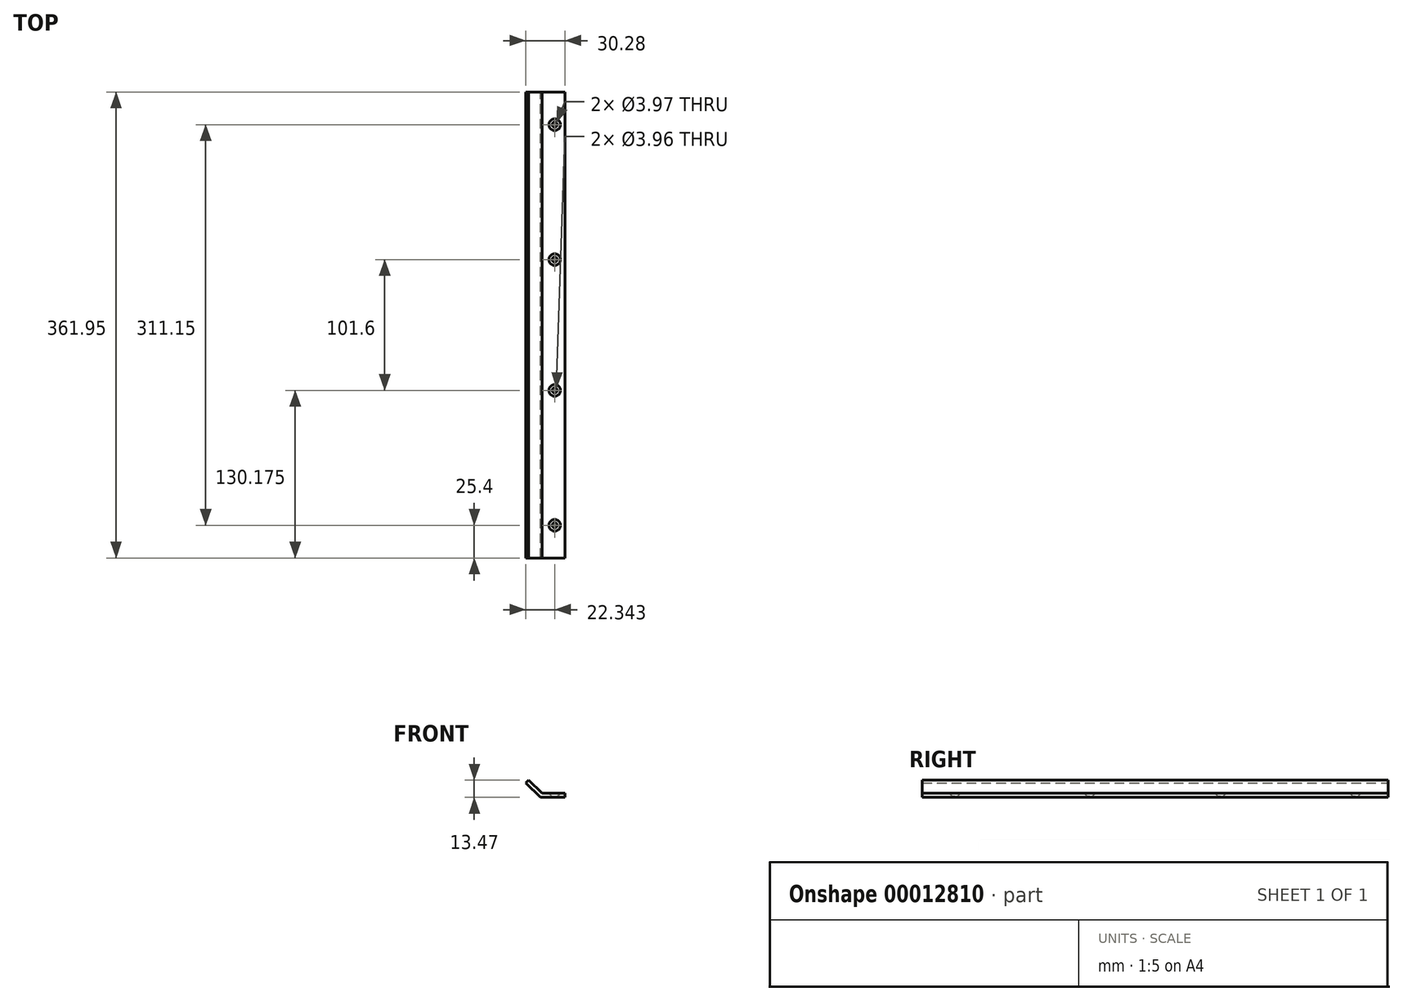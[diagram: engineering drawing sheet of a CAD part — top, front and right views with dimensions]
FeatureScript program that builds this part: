
annotation { "Feature Type Name" : "Feature", "Feature Type Description" : "" }
export const myFeature = defineFeature(function(context is Context, id is Id, definition is map)
    precondition{}
    {
        {
            var Q0;
            Q0=qCreatedBy(makeId("Front.planeOp"),FACE);
            var sketch = newSketch(context, id + "F0", { "sketchPlane" : qUnion([Q0])});
            skLineSegment(sketch, "E0", {"start": v(0, 0) * mm, "end": v(-19.05, 0) * mm});
            skLineSegment(sketch, "E1", {"start": v(-19.05, 0) * mm, "end": v(-30.28, 11.23) * mm});
            skLineSegment(sketch, "E2", {"start": v(-30.28, 11.23) * mm, "end": v(-28.03, 13.47) * mm});
            skLineSegment(sketch, "E3", {"start": v(-28.03, 13.47) * mm, "end": v(-17.73, 3.17) * mm});
            skLineSegment(sketch, "E4", {"start": v(-17.73, 3.17) * mm, "end": v(0, 3.17) * mm});
            skLineSegment(sketch, "E5", {"start": v(0, 3.17) * mm, "end": v(0, 0) * mm});
            skSolve(sketch);
        }
        {
            var Q0;
            Q0=makeQuery(id+"F0.imprint","IMPRINT",FACE,{"disambiguationData":[TD([[makeQuery(id+"F0.imprint","IMPRINT",EDGE,{"derivedFrom":sQuery(id+"F0.wireOp",EDGE,"E0")}),-1.0]])]});
            extrude(context, id + "F1", {"entities" : qUnion([Q0]), "depth" : 361.95 * mm});
        }
        {
            var Q0;
            Q0=makeQuery(id+"F1.opExtrude","SWEPT_FACE",FACE,{"disambiguationData":[OSD([sQuery(id+"F0.wireOp",EDGE,"E1")])]});
            var sketch = newSketch(context, id + "F2", { "sketchPlane" : qUnion([Q0])});
            skPoint(sketch, "E6.visualSharp", {"position": v(-29.35, 0) * mm});
            skArc(sketch, "E6.filletArc", {"start": v(-29.35, 6.35) * mm, "mid": v(-27.49, 1.86) * mm, "end": v(-23, 0) * mm});
            skLineSegment(sketch, "E7", {"start": v(-29.35, 6.35) * mm, "end": v(-29.35, 0) * mm});
            skLineSegment(sketch, "E8", {"start": v(-29.35, 0) * mm, "end": v(-23, 0) * mm});
            skSolve(sketch);
        }
        {
            var Q0;
            Q0=qSketchRegion(id+"F2",true);
            extrude(context, id + "F3", {"entities" : qUnion([Q0]), "operationType" : NewBodyOperationType.REMOVE, "oppositeDirection" : true, "depth" : 3.25 * mm});
        }
        {
            var Q0;
            Q0=makeQuery(id+"F1.opExtrude","SWEPT_FACE",FACE,{"disambiguationData":[OSD([sQuery(id+"F0.wireOp",EDGE,"E1")])]});
            var sketch = newSketch(context, id + "F4", { "sketchPlane" : qUnion([Q0])});
            skPoint(sketch, "E9.visualSharp", {"position": v(-29.35, 361.95) * mm});
            skArc(sketch, "E9.filletArc", {"start": v(-23, 361.95) * mm, "mid": v(-27.49, 360.1) * mm, "end": v(-29.35, 355.6) * mm});
            skLineSegment(sketch, "E10", {"start": v(-29.35, 355.6) * mm, "end": v(-29.35, 361.95) * mm});
            skLineSegment(sketch, "E11", {"start": v(-29.35, 361.95) * mm, "end": v(-23, 361.95) * mm});
            skSolve(sketch);
        }
        {
            var Q0;
            Q0=makeQuery(id+"F4.imprint","IMPRINT",FACE,{"disambiguationData":[TD([[makeQuery(id+"F4.imprint","IMPRINT",EDGE,{"derivedFrom":sQuery(id+"F4.wireOp",EDGE,"E9.filletArc")}),-1.0]])]});
            extrude(context, id + "F5", {"entities" : qUnion([Q0]), "operationType" : NewBodyOperationType.REMOVE, "oppositeDirection" : true, "depth" : 3.25 * mm});
        }
        {
            var Q0;
            Q0=makeQuery(id+"F1.opExtrude","SWEPT_FACE",FACE,{"disambiguationData":[OSD([sQuery(id+"F0.wireOp",EDGE,"E0")])]});
            var sketch = newSketch(context, id + "F6", { "sketchPlane" : qUnion([Q0])});
            skCircle(sketch, "E12", {"center": v(-7.94, 25.4) * mm, "radius": 1.98 * mm});
            skCircle(sketch, "E13", {"center": v(-7.94, 130.18) * mm, "radius": 1.98 * mm});
            skCircle(sketch, "E14.0.MirrorC", {"center": v(-7.94, 231.78) * mm, "radius": 1.98 * mm});
            skCircle(sketch, "E14.1.MirrorC", {"center": v(-7.94, 336.55) * mm, "radius": 1.98 * mm});
            skSolve(sketch);
        }
        {
            var Q0;
            Q0=qSketchRegion(id+"F6",true);
            extrude(context, id + "F7", {"entities" : qUnion([Q0]), "operationType" : NewBodyOperationType.REMOVE, "oppositeDirection" : true, "depth" : 3.25 * mm});
        }
        {
            var Q0;
            Q0=makeQuery(id+"F7.boolean.opBoolean","INTERSECT",EDGE,{"derivedFrom":[makeQuery(id+"F1.opExtrude","SWEPT_FACE",FACE,{"disambiguationData":[OSD([sQuery(id+"F0.wireOp",EDGE,"E4")])]}),makeQuery(id+"F7.opExtrude","SWEPT_FACE",FACE,{"disambiguationData":[OSD([sQuery(id+"F6.wireOp",EDGE,"E14.1.MirrorC")])]})]});
            var Q1;
            Q1=makeQuery(id+"F7.boolean.opBoolean","INTERSECT",EDGE,{"derivedFrom":[makeQuery(id+"F1.opExtrude","SWEPT_FACE",FACE,{"disambiguationData":[OSD([sQuery(id+"F0.wireOp",EDGE,"E4")])]}),makeQuery(id+"F7.opExtrude","SWEPT_FACE",FACE,{"disambiguationData":[OSD([sQuery(id+"F6.wireOp",EDGE,"E14.0.MirrorC")])]})]});
            var Q2;
            Q2=makeQuery(id+"F7.boolean.opBoolean","INTERSECT",EDGE,{"derivedFrom":[makeQuery(id+"F1.opExtrude","SWEPT_FACE",FACE,{"disambiguationData":[OSD([sQuery(id+"F0.wireOp",EDGE,"E4")])]}),makeQuery(id+"F7.opExtrude","SWEPT_FACE",FACE,{"disambiguationData":[OSD([sQuery(id+"F6.wireOp",EDGE,"E13")])]})]});
            var Q3;
            Q3=makeQuery(id+"F7.boolean.opBoolean","INTERSECT",EDGE,{"derivedFrom":[makeQuery(id+"F1.opExtrude","SWEPT_FACE",FACE,{"disambiguationData":[OSD([sQuery(id+"F0.wireOp",EDGE,"E4")])]}),makeQuery(id+"F7.opExtrude","SWEPT_FACE",FACE,{"disambiguationData":[OSD([sQuery(id+"F6.wireOp",EDGE,"E12")])]})]});
            chamfer(context, id + "F8", {"entities" : qUnion([Q0, Q1, Q2, Q3]), "width" : 2.54 * mm, "tangentPropagation" : true});
        }
    });
